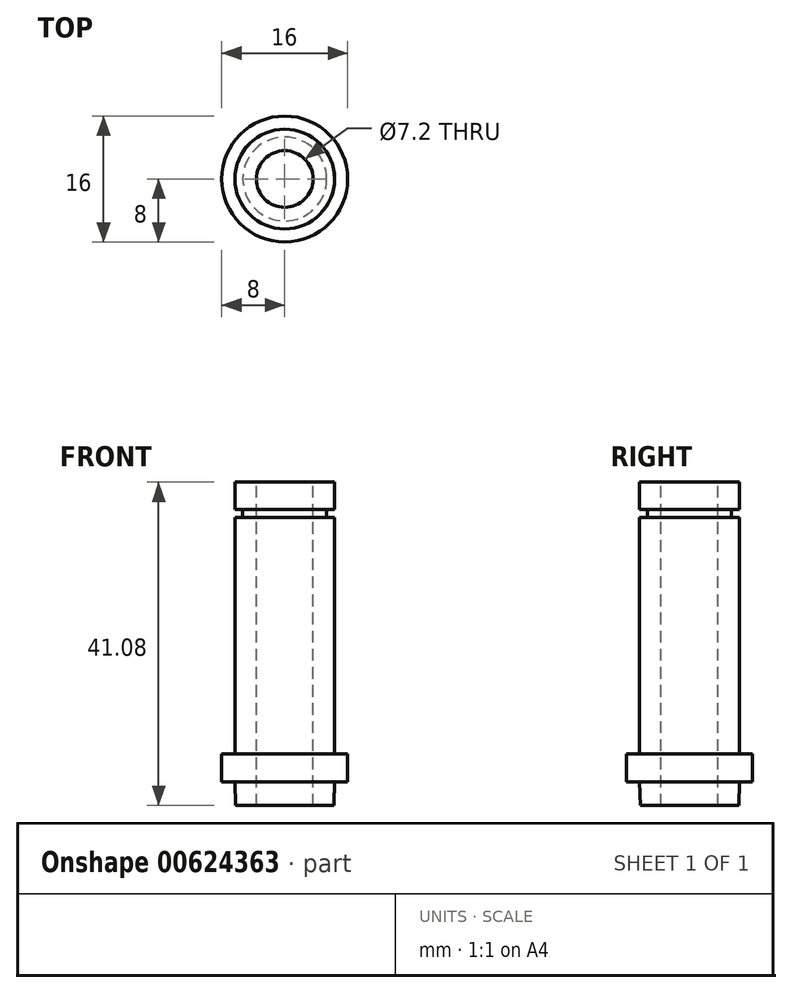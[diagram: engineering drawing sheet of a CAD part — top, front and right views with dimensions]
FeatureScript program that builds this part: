
annotation { "Feature Type Name" : "Feature", "Feature Type Description" : "" }
export const myFeature = defineFeature(function(context is Context, id is Id, definition is map)
    precondition{}
    {
        {
            var Q0;
            Q0=qCreatedBy(makeId("Right.planeOp"),FACE);
            var sketch = newSketch(context, id + "F0", { "sketchPlane" : qUnion([Q0])});
            skLineSegment(sketch, "E0", {"start": v(0, 3.48) * mm, "end": v(6.33, 3.48) * mm});
            skLineSegment(sketch, "E1", {"start": v(0, 3.48) * mm, "end": v(0, -37.6) * mm});
            skLineSegment(sketch, "E2", {"start": v(0, -37.6) * mm, "end": v(6.25, -37.6) * mm});
            skLineSegment(sketch, "E3", {"start": v(6.33, -34.62) * mm, "end": v(6.25, -37.6) * mm});
            skLineSegment(sketch, "E4", {"start": v(6.33, 3.48) * mm, "end": v(6.33, 0) * mm});
            skLineSegment(sketch, "E5", {"start": v(6.33, 0) * mm, "end": v(5.33, 0) * mm});
            skLineSegment(sketch, "E6", {"start": v(5.33, 0) * mm, "end": v(5.33, -1) * mm});
            skLineSegment(sketch, "E7", {"start": v(5.33, -1) * mm, "end": v(6.33, -1) * mm});
            skLineSegment(sketch, "E8", {"start": v(6.33, -1) * mm, "end": v(6.33, -31.02) * mm});
            skLineSegment(sketch, "E9", {"start": v(6.33, -31.02) * mm, "end": v(8, -31.02) * mm});
            skLineSegment(sketch, "E10", {"start": v(8, -31.02) * mm, "end": v(8, -34.62) * mm});
            skLineSegment(sketch, "E11", {"start": v(8, -34.62) * mm, "end": v(6.33, -34.62) * mm});
            skSolve(sketch);
        }
        {
            var Q0;
            Q0 = qSketchRegion(id + "F0", true);
            var Q1;
            Q1=sQuery(id+"F0.wireOp",EDGE,"E1");
            revolve(context, id + "F1", {"entities" : qUnion([Q0]), "axis" : qUnion([Q1]), "revolveType" : RevolveType.FULL});
        }
        {
            var Q0;
            Q0=makeQuery(id+"F1.opRevolve","SWEPT_FACE",FACE,{"disambiguationData":[OSD([sQuery(id+"F0.wireOp",EDGE,"E0")])]});
            var sketch = newSketch(context, id + "F2", { "sketchPlane" : qUnion([Q0])});
            skCircle(sketch, "E12", {"center": v(0, 0) * mm, "radius": 3.6 * mm});
            skSolve(sketch);
        }
        {
            var Q0;
            Q0 = qSketchRegion(id + "F2", true);
            extrude(context, id + "F3", {"entities" : qUnion([Q0]), "operationType" : NewBodyOperationType.REMOVE, "endBound" : BoundingType.THROUGH_ALL, "oppositeDirection" : true, "depth" : 25.4 * mm, "offsetDistance" : 25.4 * mm});
        }
    });
